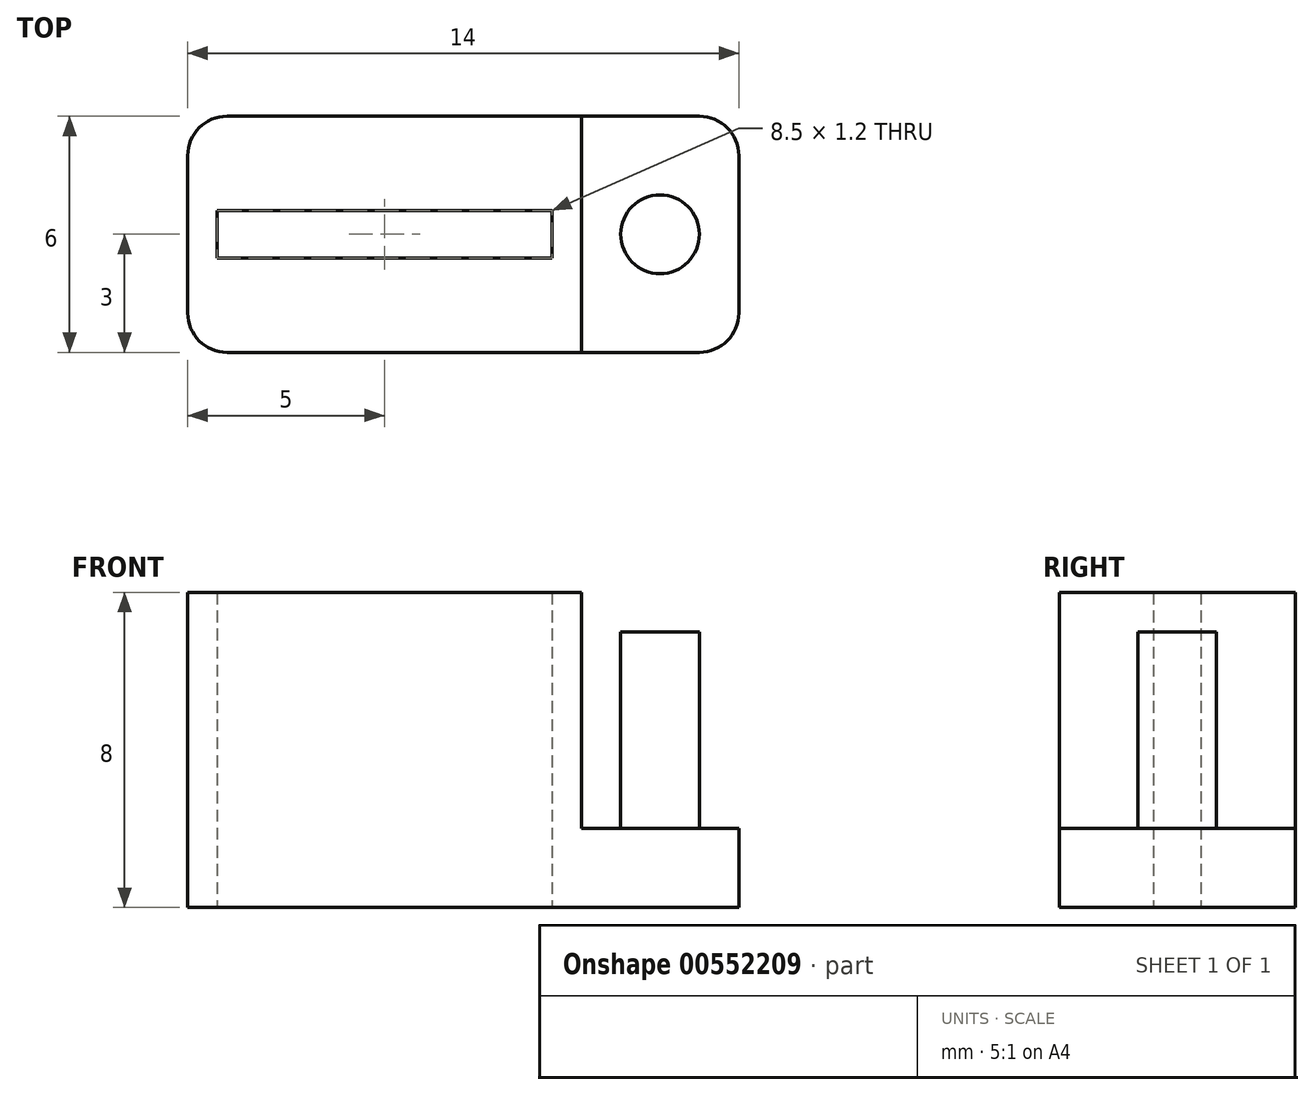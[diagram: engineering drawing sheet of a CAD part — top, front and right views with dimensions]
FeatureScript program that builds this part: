
annotation { "Feature Type Name" : "Feature", "Feature Type Description" : "" }
export const myFeature = defineFeature(function(context is Context, id is Id, definition is map)
    precondition{}
    {
        {
            var Q0;
            Q0=qCreatedBy(makeId("Top.planeOp"),FACE);
            var sketch = newSketch(context, id + "F0", { "sketchPlane" : qUnion([Q0])});
            skLineSegment(sketch, "E0.bottom", {"start": v(-5, 3) * mm, "end": v(9, 3) * mm});
            skLineSegment(sketch, "E0.top", {"start": v(-5, -3) * mm, "end": v(9, -3) * mm});
            skLineSegment(sketch, "E0.left", {"start": v(-5, 3) * mm, "end": v(-5, -3) * mm});
            skLineSegment(sketch, "E0.right", {"start": v(9, 3) * mm, "end": v(9, -3) * mm});
            skLineSegment(sketch, "E1.bottom", {"start": v(-4.25, 0.6) * mm, "end": v(4.25, 0.6) * mm});
            skLineSegment(sketch, "E1.top", {"start": v(-4.25, -0.6) * mm, "end": v(4.25, -0.6) * mm});
            skLineSegment(sketch, "E1.left", {"start": v(-4.25, 0.6) * mm, "end": v(-4.25, -0.6) * mm});
            skLineSegment(sketch, "E1.right", {"start": v(4.25, 0.6) * mm, "end": v(4.25, -0.6) * mm});
            skSolve(sketch);
        }
        {
            var Q0;
            Q0=makeQuery(id+"F0.imprint","IMPRINT",FACE,{"disambiguationData":[TD([[makeQuery(id+"F0.imprint","IMPRINT",EDGE,{"derivedFrom":sQuery(id+"F0.wireOp",EDGE,"E0.bottom")}),-1.0]])]});
            extrude(context, id + "F1", {"entities" : qUnion([Q0]), "depth" : 8 * mm, "offsetDistance" : 25 * mm});
        }
        {
            var Q0;
            Q0=makeQuery(id+"F1.opExtrude","CAP_FACE",FACE,{"disambiguationData":[OSD([sQuery(id+"F0.wireOp",EDGE,"E0.bottom"),sQuery(id+"F0.wireOp",EDGE,"E0.top"),sQuery(id+"F0.wireOp",EDGE,"E0.left"),sQuery(id+"F0.wireOp",EDGE,"E0.right"),sQuery(id+"F0.wireOp",EDGE,"E1.bottom"),sQuery(id+"F0.wireOp",EDGE,"E1.top"),sQuery(id+"F0.wireOp",EDGE,"E1.left"),sQuery(id+"F0.wireOp",EDGE,"E1.right")])],"isStart":false});
            var sketch = newSketch(context, id + "F2", { "sketchPlane" : qUnion([Q0])});
            skLineSegment(sketch, "E2.bottom", {"start": v(5, 3) * mm, "end": v(9, 3) * mm});
            skLineSegment(sketch, "E2.top", {"start": v(5, -3) * mm, "end": v(9, -3) * mm});
            skLineSegment(sketch, "E2.left", {"start": v(5, 3) * mm, "end": v(5, -3) * mm});
            skLineSegment(sketch, "E2.right", {"start": v(9, 3) * mm, "end": v(9, -3) * mm});
            skSolve(sketch);
        }
        {
            var Q0;
            Q0=makeQuery(id+"F2.imprint","IMPRINT",FACE,{"disambiguationData":[TD([[makeQuery(id+"F2.imprint","IMPRINT",EDGE,{"derivedFrom":sQuery(id+"F2.wireOp",EDGE,"E2.bottom")}),-1.0]])]});
            extrude(context, id + "F3", {"entities" : qUnion([Q0]), "operationType" : NewBodyOperationType.REMOVE, "oppositeDirection" : true, "depth" : 6 * mm, "offsetDistance" : 25 * mm});
        }
        {
            var Q0;
            Q0=makeQuery(id+"F3.boolean.opBoolean","COPY",FACE,{"derivedFrom":makeQuery(id+"F3.opExtrude","CAP_FACE",FACE,{"disambiguationData":[OSD([sQuery(id+"F2.wireOp",EDGE,"E2.bottom"),sQuery(id+"F2.wireOp",EDGE,"E2.top"),sQuery(id+"F2.wireOp",EDGE,"E2.left"),sQuery(id+"F2.wireOp",EDGE,"E2.right")])],"isStart":false})});
            var sketch = newSketch(context, id + "F4", { "sketchPlane" : qUnion([Q0])});
            skCircle(sketch, "E3", {"center": v(7, 0) * mm, "radius": 1 * mm});
            skSolve(sketch);
        }
        {
            var Q0;
            Q0=makeQuery(id+"F4.imprint","IMPRINT",FACE,{"disambiguationData":[TD([[makeQuery(id+"F4.imprint","IMPRINT",EDGE,{"derivedFrom":sQuery(id+"F4.wireOp",EDGE,"E3")}),1.0]])]});
            extrude(context, id + "F5", {"entities" : qUnion([Q0]), "operationType" : NewBodyOperationType.ADD, "depth" : 5 * mm, "offsetDistance" : 25 * mm});
        }
        {
            var Q0;
            Q0=makeQuery(id+"F3.boolean.opBoolean","COPY",EDGE,{"derivedFrom":makeQuery(id+"F3.opExtrude","SWEPT_EDGE",EDGE,{"disambiguationData":[OSD([sQuery(id+"F0.wireOp",EDGE,"E0.bottom"),sQuery(id+"F2.wireOp",EDGE,"E2.bottom"),sQuery(id+"F2.wireOp",EDGE,"E2.left")])]})});
            var Q1;
            Q1=makeQuery(id+"F3.boolean.opBoolean","COPY",EDGE,{"derivedFrom":makeQuery(id+"F3.opExtrude","SWEPT_EDGE",EDGE,{"disambiguationData":[OSD([sQuery(id+"F0.wireOp",EDGE,"E0.top"),sQuery(id+"F2.wireOp",EDGE,"E2.top"),sQuery(id+"F2.wireOp",EDGE,"E2.left")])]})});
            var Q2;
            Q2=makeQuery(id+"F1.opExtrude","SWEPT_EDGE",EDGE,{"disambiguationData":[OSD([sQuery(id+"F0.wireOp",EDGE,"E0.top"),sQuery(id+"F0.wireOp",EDGE,"E0.right")])]});
            var Q3;
            Q3=makeQuery(id+"F1.opExtrude","SWEPT_EDGE",EDGE,{"disambiguationData":[OSD([sQuery(id+"F0.wireOp",EDGE,"E0.bottom"),sQuery(id+"F0.wireOp",EDGE,"E0.right")])]});
            var Q4;
            Q4=makeQuery(id+"F1.opExtrude","SWEPT_EDGE",EDGE,{"disambiguationData":[OSD([sQuery(id+"F0.wireOp",EDGE,"E0.bottom"),sQuery(id+"F0.wireOp",EDGE,"E0.left")])]});
            var Q5;
            Q5=makeQuery(id+"F1.opExtrude","SWEPT_EDGE",EDGE,{"disambiguationData":[OSD([sQuery(id+"F0.wireOp",EDGE,"E0.top"),sQuery(id+"F0.wireOp",EDGE,"E0.left")])]});
            fillet(context, id + "F6", {"entities" : qUnion([Q0, Q1, Q2, Q3, Q4, Q5]), "radius" : 1 * mm, "tangentPropagation" : true, "allowEdgeOverflow" : false});
        }
    });
